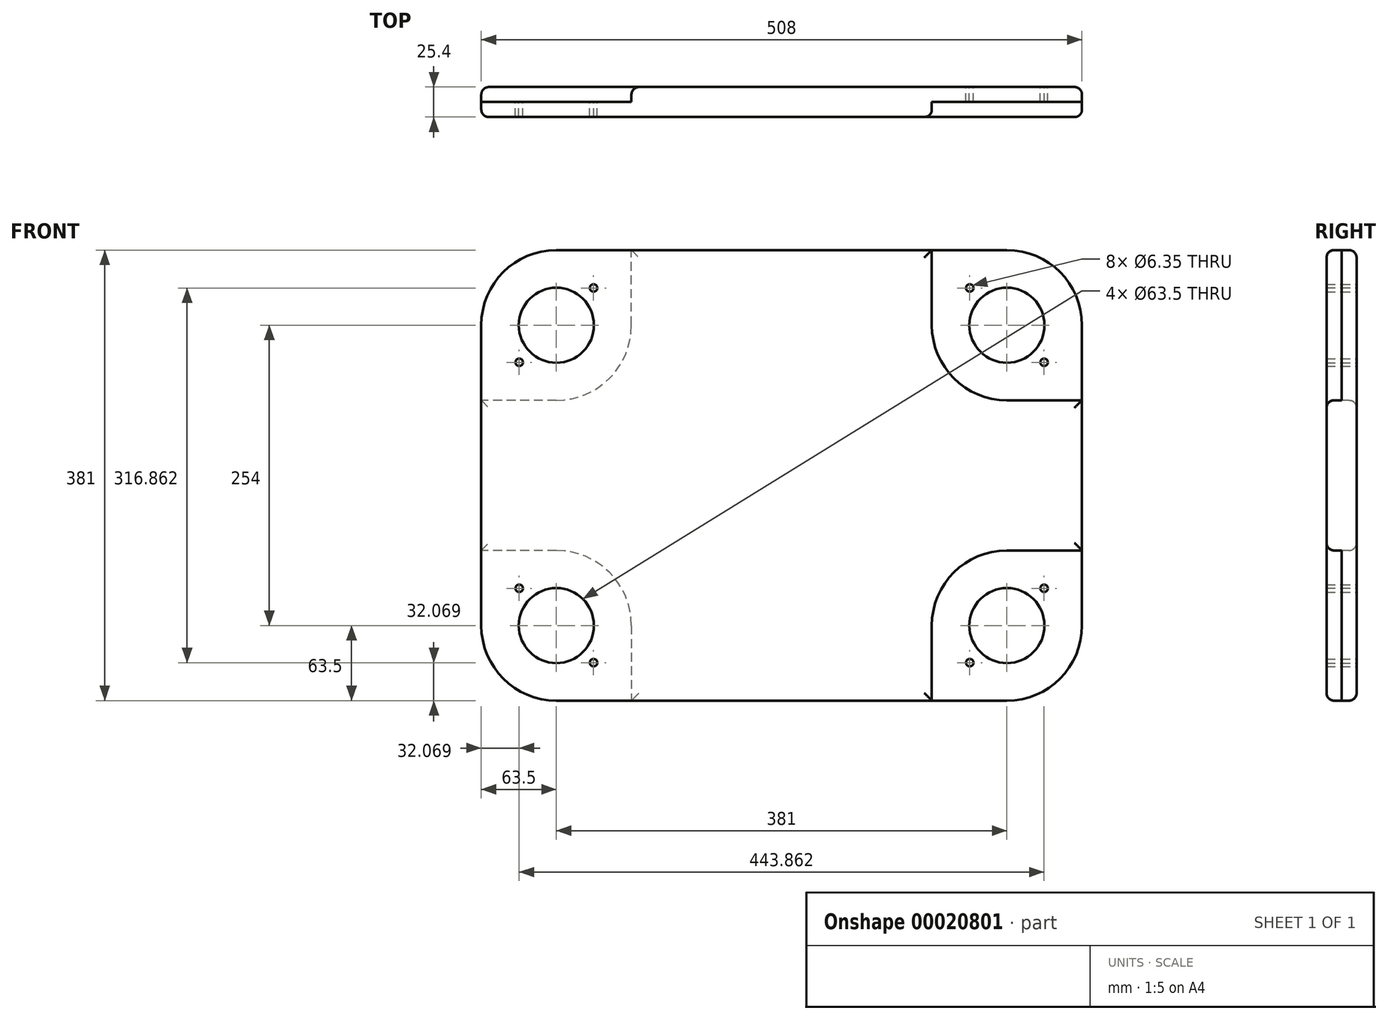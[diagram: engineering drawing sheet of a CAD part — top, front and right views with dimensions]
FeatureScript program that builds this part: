
annotation { "Feature Type Name" : "Feature", "Feature Type Description" : "" }
export const myFeature = defineFeature(function(context is Context, id is Id, definition is map)
    precondition{}
    {
        {
            var Q0;
            Q0=qCreatedBy(makeId("Front.planeOp"),FACE);
            var sketch = newSketch(context, id + "F0", { "sketchPlane" : qUnion([Q0])});
            skLineSegment(sketch, "E0.rect.bottom", {"start": v(190.5, -190.5) * mm, "end": v(-190.5, -190.5) * mm});
            skLineSegment(sketch, "E0.rect.top", {"start": v(190.5, 190.5) * mm, "end": v(-190.5, 190.5) * mm});
            skLineSegment(sketch, "E0.rect.left", {"start": v(254, -127) * mm, "end": v(254, 127) * mm});
            skLineSegment(sketch, "E0.rect.right", {"start": v(-254, -127) * mm, "end": v(-254, 127) * mm});
            skPoint(sketch, "E0.rect.middle", {"position": v(0, 0) * mm});
            skPoint(sketch, "E1.orphan", {"position": v(254, 254) * mm});
            skPoint(sketch, "E2.orphan", {"position": v(-254, 190.5) * mm});
            skPoint(sketch, "E3.orphan", {"position": v(-254, -254) * mm});
            skPoint(sketch, "E4.orphan", {"position": v(254, -190.5) * mm});
            skCircle(sketch, "E5", {"center": v(-190.5, 127) * mm, "radius": 31.75 * mm});
            skCircle(sketch, "E6.0.1.0", {"center": v(-190.5, -127) * mm, "radius": 31.75 * mm});
            skCircle(sketch, "E6.1.0.0", {"center": v(190.5, 127) * mm, "radius": 31.75 * mm});
            skCircle(sketch, "E6.1.1.0", {"center": v(190.5, -127) * mm, "radius": 31.75 * mm});
            skLineSegment(sketch, "E7", {"start": v(190.5, -127) * mm, "end": v(254, -127) * mm, "construction": true});
            skLineSegment(sketch, "E8", {"start": v(-190.5, -127) * mm, "end": v(-254, -127) * mm, "construction": true});
            skLineSegment(sketch, "E9", {"start": v(190.5, -127) * mm, "end": v(190.5, -190.5) * mm, "construction": true});
            skLineSegment(sketch, "E10", {"start": v(190.5, 127) * mm, "end": v(190.5, 190.5) * mm, "construction": true});
            skArc(sketch, "E11", {"start": v(190.5, -63.5) * mm, "mid": v(145.6, -82.1) * mm, "end": v(127, -127) * mm});
            skArc(sketch, "E12", {"start": v(254, 127) * mm, "mid": v(235.4, 171.9) * mm, "end": v(190.5, 190.5) * mm});
            skArc(sketch, "E13", {"start": v(-127, -127) * mm, "mid": v(-145.6, -82.1) * mm, "end": v(-190.5, -63.5) * mm});
            skArc(sketch, "E14", {"start": v(-190.5, 190.5) * mm, "mid": v(-235.4, 171.9) * mm, "end": v(-254, 127) * mm});
            skLineSegment(sketch, "E15", {"start": v(127, -127) * mm, "end": v(127, -190.5) * mm});
            skLineSegment(sketch, "E16", {"start": v(190.5, -63.5) * mm, "end": v(254, -63.5) * mm});
            skArc(sketch, "E17.trimOffspring", {"start": v(190.5, -190.5) * mm, "mid": v(235.4, -171.9) * mm, "end": v(254, -127) * mm});
            skLineSegment(sketch, "E18", {"start": v(190.5, 63.5) * mm, "end": v(254, 63.5) * mm});
            skPoint(sketch, "E18.startSnap0", {"position": v(254, 63.5) * mm});
            skLineSegment(sketch, "E19", {"start": v(127, 127) * mm, "end": v(127, 190.5) * mm});
            skArc(sketch, "E20.trimOffspring", {"start": v(127, 127) * mm, "mid": v(145.6, 82.1) * mm, "end": v(190.5, 63.5) * mm});
            skLineSegment(sketch, "E21", {"start": v(-127, 127) * mm, "end": v(-127, 190.5) * mm});
            skLineSegment(sketch, "E22", {"start": v(-190.5, 63.5) * mm, "end": v(-254, 63.5) * mm});
            skArc(sketch, "E23.trimOffspring", {"start": v(-190.5, 63.5) * mm, "mid": v(-145.6, 82.1) * mm, "end": v(-127, 127) * mm});
            skLineSegment(sketch, "E24", {"start": v(-127, -127) * mm, "end": v(-127, -190.5) * mm});
            skLineSegment(sketch, "E25", {"start": v(-190.5, -63.5) * mm, "end": v(-254, -63.5) * mm});
            skArc(sketch, "E26.trimOffspring", {"start": v(-254, -127) * mm, "mid": v(-235.4, -171.9) * mm, "end": v(-190.5, -190.5) * mm});
            skCircle(sketch, "E27", {"center": v(159.07, 158.43) * mm, "radius": 3.18 * mm});
            skCircle(sketch, "E28", {"center": v(221.93, 95.57) * mm, "radius": 3.18 * mm});
            skCircle(sketch, "E29", {"center": v(159.07, -158.43) * mm, "radius": 3.18 * mm});
            skCircle(sketch, "E30", {"center": v(221.93, -95.57) * mm, "radius": 3.18 * mm});
            skCircle(sketch, "E31", {"center": v(-221.93, -95.57) * mm, "radius": 3.18 * mm});
            skCircle(sketch, "E32", {"center": v(-159.07, -158.43) * mm, "radius": 3.18 * mm});
            skCircle(sketch, "E33", {"center": v(-221.93, 95.57) * mm, "radius": 3.18 * mm});
            skCircle(sketch, "E34", {"center": v(-159.07, 158.43) * mm, "radius": 3.18 * mm});
            skLineSegment(sketch, "E35", {"start": v(-127, 190.5) * mm, "end": v(-254, 63.5) * mm, "construction": true});
            skLineSegment(sketch, "E36", {"start": v(-254, -63.5) * mm, "end": v(-127, -190.5) * mm, "construction": true});
            skLineSegment(sketch, "E37", {"start": v(127, 190.5) * mm, "end": v(254, 63.5) * mm, "construction": true});
            skLineSegment(sketch, "E38", {"start": v(254, -63.5) * mm, "end": v(127, -190.5) * mm, "construction": true});
            skSolve(sketch);
        }
        {
            var Q0;
            Q0 = qSketchRegion(id + "F0", true);
            extrude(context, id + "F1", {"entities" : qUnion([Q0]), "endBound" : BoundingType.SYMMETRIC, "depth" : 25.4 * mm});
        }
        {
            var Q0;
            Q0=makeQuery(id+"F0.imprint","IMPRINT",FACE,{"disambiguationData":[TD([[makeQuery(id+"F0.imprint","IMPRINT",EDGE,{"derivedFrom":sQuery(id+"F0.wireOp",EDGE,"E6.0.1.0")}),-1.0]])]});
            var Q1;
            Q1=makeQuery(id+"F0.imprint","IMPRINT",FACE,{"disambiguationData":[TD([[makeQuery(id+"F0.imprint","IMPRINT",EDGE,{"derivedFrom":sQuery(id+"F0.wireOp",EDGE,"E5")}),-1.0]])]});
            extrude(context, id + "F2", {"entities" : qUnion([Q0, Q1]), "operationType" : NewBodyOperationType.REMOVE, "endBound" : BoundingType.THROUGH_ALL, "oppositeDirection" : true, "depth" : 25.4 * mm});
        }
        {
            var Q0;
            Q0=makeQuery(id+"F0.imprint","IMPRINT",FACE,{"disambiguationData":[TD([[makeQuery(id+"F0.imprint","IMPRINT",EDGE,{"derivedFrom":sQuery(id+"F0.wireOp",EDGE,"E6.1.1.0")}),-1.0]])]});
            var Q1;
            Q1=makeQuery(id+"F0.imprint","IMPRINT",FACE,{"disambiguationData":[TD([[makeQuery(id+"F0.imprint","IMPRINT",EDGE,{"derivedFrom":sQuery(id+"F0.wireOp",EDGE,"E6.1.0.0")}),-1.0]])]});
            extrude(context, id + "F3", {"entities" : qUnion([Q0, Q1]), "operationType" : NewBodyOperationType.REMOVE, "endBound" : BoundingType.THROUGH_ALL, "depth" : 25.4 * mm});
        }
        {
            var Q0;
            Q0=makeQuery(id+"F1.opExtrude","CAP_EDGE",EDGE,{"disambiguationData":[OSD([sQuery(id+"F0.wireOp",EDGE,"E0.rect.right")])],"isStart":true});
            var Q1;
            Q1=makeQuery(id+"F2.boolean.opBoolean","INTERSECT",EDGE,{"derivedFrom":[makeQuery(id+"F1.opExtrude","CAP_FACE",FACE,{"disambiguationData":[OSD([sQuery(id+"F0.wireOp",EDGE,"E0.rect.bottom"),sQuery(id+"F0.wireOp",EDGE,"E0.rect.top"),sQuery(id+"F0.wireOp",EDGE,"E0.rect.left"),sQuery(id+"F0.wireOp",EDGE,"E0.rect.right"),sQuery(id+"F0.wireOp",EDGE,"E5"),sQuery(id+"F0.wireOp",EDGE,"E6.0.1.0"),sQuery(id+"F0.wireOp",EDGE,"E6.1.0.0"),sQuery(id+"F0.wireOp",EDGE,"E6.1.1.0"),sQuery(id+"F0.wireOp",EDGE,"E12"),sQuery(id+"F0.wireOp",EDGE,"E14"),sQuery(id+"F0.wireOp",EDGE,"E17.trimOffspring"),sQuery(id+"F0.wireOp",EDGE,"E26.trimOffspring"),sQuery(id+"F0.wireOp",EDGE,"E27"),sQuery(id+"F0.wireOp",EDGE,"E28"),sQuery(id+"F0.wireOp",EDGE,"E29"),sQuery(id+"F0.wireOp",EDGE,"E30"),sQuery(id+"F0.wireOp",EDGE,"E31"),sQuery(id+"F0.wireOp",EDGE,"E32"),sQuery(id+"F0.wireOp",EDGE,"E33"),sQuery(id+"F0.wireOp",EDGE,"E34")])],"isStart":true}),makeQuery(id+"F2.opExtrude","SWEPT_FACE",FACE,{"disambiguationData":[OSD([sQuery(id+"F0.wireOp",EDGE,"E25")])]})]});
            var Q2;
            Q2=makeQuery(id+"F1.opExtrude","CAP_EDGE",EDGE,{"disambiguationData":[OSD([sQuery(id+"F0.wireOp",EDGE,"E0.rect.bottom")])],"isStart":true});
            var Q3;
            Q3=makeQuery(id+"F2.boolean.opBoolean","INTERSECT",EDGE,{"derivedFrom":[makeQuery(id+"F1.opExtrude","CAP_FACE",FACE,{"disambiguationData":[OSD([sQuery(id+"F0.wireOp",EDGE,"E0.rect.bottom"),sQuery(id+"F0.wireOp",EDGE,"E0.rect.top"),sQuery(id+"F0.wireOp",EDGE,"E0.rect.left"),sQuery(id+"F0.wireOp",EDGE,"E0.rect.right"),sQuery(id+"F0.wireOp",EDGE,"E5"),sQuery(id+"F0.wireOp",EDGE,"E6.0.1.0"),sQuery(id+"F0.wireOp",EDGE,"E6.1.0.0"),sQuery(id+"F0.wireOp",EDGE,"E6.1.1.0"),sQuery(id+"F0.wireOp",EDGE,"E12"),sQuery(id+"F0.wireOp",EDGE,"E14"),sQuery(id+"F0.wireOp",EDGE,"E17.trimOffspring"),sQuery(id+"F0.wireOp",EDGE,"E26.trimOffspring"),sQuery(id+"F0.wireOp",EDGE,"E27"),sQuery(id+"F0.wireOp",EDGE,"E28"),sQuery(id+"F0.wireOp",EDGE,"E29"),sQuery(id+"F0.wireOp",EDGE,"E30"),sQuery(id+"F0.wireOp",EDGE,"E31"),sQuery(id+"F0.wireOp",EDGE,"E32"),sQuery(id+"F0.wireOp",EDGE,"E33"),sQuery(id+"F0.wireOp",EDGE,"E34")])],"isStart":true}),makeQuery(id+"F2.opExtrude","SWEPT_FACE",FACE,{"disambiguationData":[OSD([sQuery(id+"F0.wireOp",EDGE,"E21")])]})]});
            var Q4;
            Q4=makeQuery(id+"F1.opExtrude","CAP_EDGE",EDGE,{"disambiguationData":[OSD([sQuery(id+"F0.wireOp",EDGE,"E0.rect.left")])],"isStart":false});
            var Q5;
            Q5=makeQuery(id+"F3.boolean.opBoolean","INTERSECT",EDGE,{"derivedFrom":[makeQuery(id+"F1.opExtrude","CAP_FACE",FACE,{"disambiguationData":[OSD([sQuery(id+"F0.wireOp",EDGE,"E0.rect.bottom"),sQuery(id+"F0.wireOp",EDGE,"E0.rect.top"),sQuery(id+"F0.wireOp",EDGE,"E0.rect.left"),sQuery(id+"F0.wireOp",EDGE,"E0.rect.right"),sQuery(id+"F0.wireOp",EDGE,"E5"),sQuery(id+"F0.wireOp",EDGE,"E6.0.1.0"),sQuery(id+"F0.wireOp",EDGE,"E6.1.0.0"),sQuery(id+"F0.wireOp",EDGE,"E6.1.1.0"),sQuery(id+"F0.wireOp",EDGE,"E12"),sQuery(id+"F0.wireOp",EDGE,"E14"),sQuery(id+"F0.wireOp",EDGE,"E17.trimOffspring"),sQuery(id+"F0.wireOp",EDGE,"E26.trimOffspring"),sQuery(id+"F0.wireOp",EDGE,"E27"),sQuery(id+"F0.wireOp",EDGE,"E28"),sQuery(id+"F0.wireOp",EDGE,"E29"),sQuery(id+"F0.wireOp",EDGE,"E30"),sQuery(id+"F0.wireOp",EDGE,"E31"),sQuery(id+"F0.wireOp",EDGE,"E32"),sQuery(id+"F0.wireOp",EDGE,"E33"),sQuery(id+"F0.wireOp",EDGE,"E34")])],"isStart":false}),makeQuery(id+"F3.opExtrude","SWEPT_FACE",FACE,{"disambiguationData":[OSD([sQuery(id+"F0.wireOp",EDGE,"E16")])]})]});
            var Q6;
            Q6=makeQuery(id+"F1.opExtrude","CAP_EDGE",EDGE,{"disambiguationData":[OSD([sQuery(id+"F0.wireOp",EDGE,"E0.rect.bottom")])],"isStart":false});
            var Q7;
            Q7=makeQuery(id+"F3.boolean.opBoolean","INTERSECT",EDGE,{"derivedFrom":[makeQuery(id+"F1.opExtrude","CAP_FACE",FACE,{"disambiguationData":[OSD([sQuery(id+"F0.wireOp",EDGE,"E0.rect.bottom"),sQuery(id+"F0.wireOp",EDGE,"E0.rect.top"),sQuery(id+"F0.wireOp",EDGE,"E0.rect.left"),sQuery(id+"F0.wireOp",EDGE,"E0.rect.right"),sQuery(id+"F0.wireOp",EDGE,"E5"),sQuery(id+"F0.wireOp",EDGE,"E6.0.1.0"),sQuery(id+"F0.wireOp",EDGE,"E6.1.0.0"),sQuery(id+"F0.wireOp",EDGE,"E6.1.1.0"),sQuery(id+"F0.wireOp",EDGE,"E12"),sQuery(id+"F0.wireOp",EDGE,"E14"),sQuery(id+"F0.wireOp",EDGE,"E17.trimOffspring"),sQuery(id+"F0.wireOp",EDGE,"E26.trimOffspring"),sQuery(id+"F0.wireOp",EDGE,"E27"),sQuery(id+"F0.wireOp",EDGE,"E28"),sQuery(id+"F0.wireOp",EDGE,"E29"),sQuery(id+"F0.wireOp",EDGE,"E30"),sQuery(id+"F0.wireOp",EDGE,"E31"),sQuery(id+"F0.wireOp",EDGE,"E32"),sQuery(id+"F0.wireOp",EDGE,"E33"),sQuery(id+"F0.wireOp",EDGE,"E34")])],"isStart":false}),makeQuery(id+"F3.opExtrude","SWEPT_FACE",FACE,{"disambiguationData":[OSD([sQuery(id+"F0.wireOp",EDGE,"E18")])]})]});
            fillet(context, id + "F4", {"entities" : qUnion([Q0, Q1, Q2, Q3, Q4, Q5, Q6, Q7]), "radius" : 6.35 * mm, "tangentPropagation" : true, "allowEdgeOverflow" : false});
        }
    });
